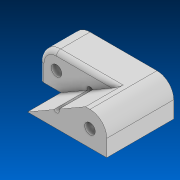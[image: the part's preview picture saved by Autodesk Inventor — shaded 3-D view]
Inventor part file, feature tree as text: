
AUTODESK INVENTOR PART (.ipt)
format: ipt  version: 2022.2 (Build 262287000, 287)  size: 136,704 bytes
history: native  units: in
note: dims shown in document units (in); Inventor stores cm internally (conversion verified against a paired STEP export)
features: hole x3, sketch x2, extrude x2, fillet x2
ambient origin geometry x8: Origin, YZ Plane, XZ Plane, XY Plane, X Axis, Y Axis, Z Axis, Center Point
bodies: Solid1 (feature_tree)
feature tree (9):
  sketch  "Sketch1"  dims[d0=1.0in d1=1.0in]
  extrude  "Extrusion1"  Depth=1.0in
  extrude  "Extrusion2"  Depth=0.5in
  hole  "Hole1"  [1 undecoded]
  hole  "Hole2"  [1 undecoded]
  fillet  "Fillet2"  Radius=1.0in
  fillet  "Fillet1"  Radius=0.125in
  hole  "Hole3"  [1 undecoded]
  sketch  "Sketch2"  dims[d2=1.0in d3=0.5in d4=30.0deg d5=1.0in d6=0.0in d7=1.0in d8=0.0in d9=0.125in d13=0.175in d14=0.75in d15=0.22in d16=0.325in d17=0.5635in d18=1.5in d19=0.0in d20=0.175in d21=0.75in d22=0.315in d23=0.5in d24=0.5635in d25=1.0in d26=0.0in d27=0.5in d28=0.175in d29=0.75in d30=0.315in d31=0.15in d32=0.5635in d33=1.0in d34=0.8108in]
note: 3 required parameter values undecoded (feature->parameter linkage not recoverable at this tier; creation-order binding heuristic only, values carry confidence <= 0.55)
